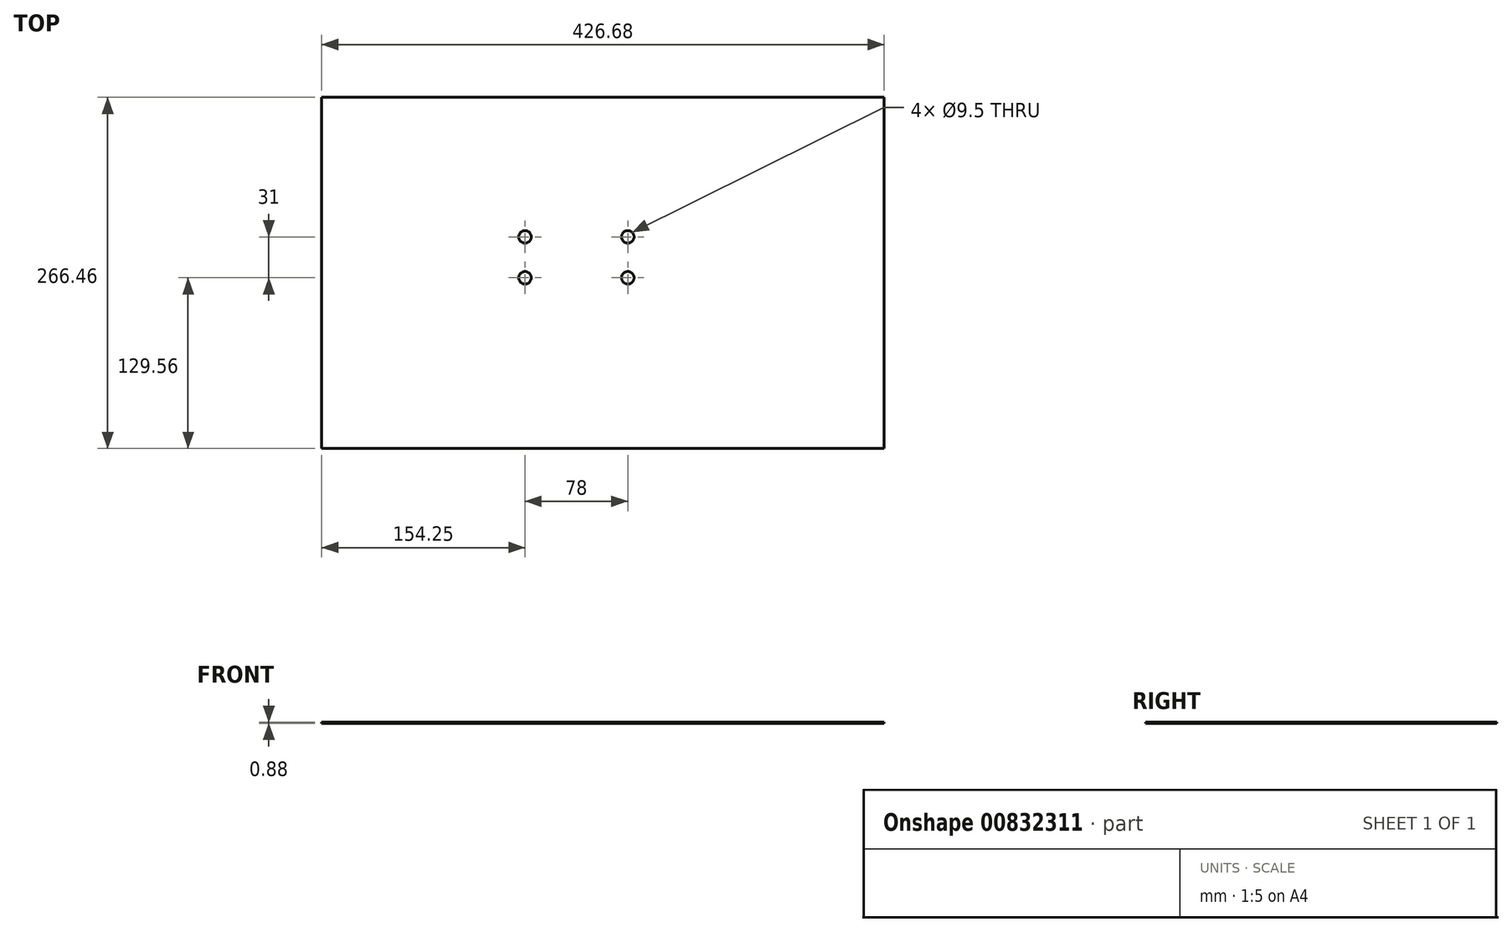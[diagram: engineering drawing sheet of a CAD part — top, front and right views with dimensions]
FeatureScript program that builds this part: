
annotation { "Feature Type Name" : "Feature", "Feature Type Description" : "" }
export const myFeature = defineFeature(function(context is Context, id is Id, definition is map)
    precondition{}
    {
        {
            var Q0;
            Q0=qCreatedBy(makeId("Top.planeOp"),FACE);
            var sketch = newSketch(context, id + "F0", { "sketchPlane" : qUnion([Q0])});
            skLineSegment(sketch, "E0.bottom", {"start": v(-198.5, 128.15) * mm, "end": v(228.18, 128.15) * mm});
            skLineSegment(sketch, "E0.top", {"start": v(-198.5, -138.3) * mm, "end": v(228.18, -138.3) * mm});
            skLineSegment(sketch, "E0.left", {"start": v(-198.5, 128.15) * mm, "end": v(-198.5, -138.3) * mm});
            skLineSegment(sketch, "E0.right", {"start": v(228.18, 128.15) * mm, "end": v(228.18, -138.3) * mm});
            skLineSegment(sketch, "E1", {"start": v(-224.35, 22.25) * mm, "end": v(262.47, 22.25) * mm, "construction": true});
            skLineSegment(sketch, "E2", {"start": v(-215.92, -8.75) * mm, "end": v(258.53, -8.75) * mm, "construction": true});
            skLineSegment(sketch, "E3", {"start": v(-44.25, 149.38) * mm, "end": v(-44.25, -162.05) * mm, "construction": true});
            skLineSegment(sketch, "E4", {"start": v(33.75, 158.94) * mm, "end": v(33.75, -182.29) * mm, "construction": true});
            skCircle(sketch, "E5", {"center": v(-44.25, 22.25) * mm, "radius": 4.75 * mm});
            skCircle(sketch, "E6", {"center": v(33.75, 22.25) * mm, "radius": 4.75 * mm});
            skCircle(sketch, "E7", {"center": v(33.75, -8.75) * mm, "radius": 4.75 * mm});
            skCircle(sketch, "E8", {"center": v(-44.25, -8.75) * mm, "radius": 4.75 * mm});
            skSolve(sketch);
        }
        {
            var Q0;
            Q0 = qSketchRegion(id + "F0", true);
            extrude(context, id + "F1", {"entities" : qUnion([Q0]), "depth" : .88 * mm, "offsetDistance" : 25 * mm});
        }
    });
